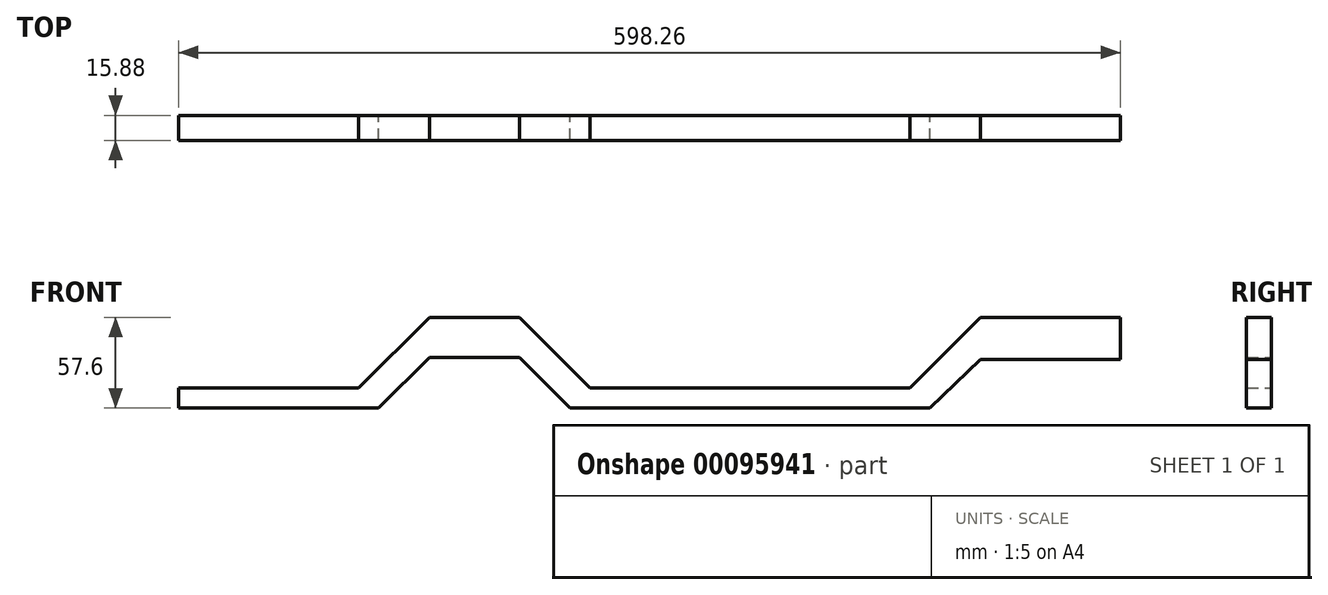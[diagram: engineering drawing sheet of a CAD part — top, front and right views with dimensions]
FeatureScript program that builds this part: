
annotation { "Feature Type Name" : "Feature", "Feature Type Description" : "" }
export const myFeature = defineFeature(function(context is Context, id is Id, definition is map)
    precondition{}
    {
        {
            var Q0;
            Q0=qCreatedBy(makeId("Front.planeOp"),FACE);
            var sketch = newSketch(context, id + "F0", { "sketchPlane" : qUnion([Q0])});
            skLineSegment(sketch, "E0", {"start": v(-232.76, -81.83) * mm, "end": v(-105.76, -81.83) * mm});
            skLineSegment(sketch, "E1", {"start": v(-105.76, -81.83) * mm, "end": v(-118.46, -69.13) * mm});
            skLineSegment(sketch, "E2", {"start": v(-118.46, -69.13) * mm, "end": v(-232.76, -69.13) * mm});
            skLineSegment(sketch, "E3", {"start": v(-118.46, -69.13) * mm, "end": v(-73.56, -24.23) * mm});
            skLineSegment(sketch, "E4", {"start": v(-105.76, -81.83) * mm, "end": v(-73.56, -49.63) * mm});
            skLineSegment(sketch, "E5", {"start": v(-73.56, -24.23) * mm, "end": v(-73.56, -49.63) * mm});
            skLineSegment(sketch, "E6", {"start": v(-73.56, -24.23) * mm, "end": v(-16.4, -24.23) * mm});
            skLineSegment(sketch, "E7", {"start": v(-73.56, -49.63) * mm, "end": v(-16.4, -49.63) * mm});
            skLineSegment(sketch, "E8", {"start": v(-16.4, -24.23) * mm, "end": v(-16.4, -49.63) * mm});
            skLineSegment(sketch, "E9", {"start": v(-16.4, -24.23) * mm, "end": v(28.5, -69.13) * mm});
            skLineSegment(sketch, "E10", {"start": v(28.5, -69.13) * mm, "end": v(53.9, -69.13) * mm});
            skLineSegment(sketch, "E11", {"start": v(53.9, -81.83) * mm, "end": v(15.8, -81.83) * mm});
            skLineSegment(sketch, "E12", {"start": v(15.8, -81.83) * mm, "end": v(28.5, -69.13) * mm});
            skLineSegment(sketch, "E13", {"start": v(-16.4, -49.63) * mm, "end": v(15.8, -81.83) * mm});
            skLineSegment(sketch, "E14", {"start": v(53.9, -81.83) * mm, "end": v(244.4, -81.83) * mm});
            skLineSegment(sketch, "E15", {"start": v(231.7, -69.14) * mm, "end": v(244.4, -81.83) * mm});
            skLineSegment(sketch, "E16", {"start": v(-232.76, -69.13) * mm, "end": v(-232.76, -81.83) * mm});
            skLineSegment(sketch, "E17", {"start": v(53.9, -69.13) * mm, "end": v(231.7, -69.14) * mm});
            skLineSegment(sketch, "E18", {"start": v(231.7, -69.14) * mm, "end": v(276.6, -24.23) * mm});
            skLineSegment(sketch, "E19", {"start": v(276.6, -24.23) * mm, "end": v(365.5, -24.23) * mm});
            skLineSegment(sketch, "E20", {"start": v(244.4, -81.83) * mm, "end": v(276.6, -50.74) * mm});
            skLineSegment(sketch, "E21", {"start": v(276.6, -24.23) * mm, "end": v(276.6, -50.74) * mm});
            skLineSegment(sketch, "E22", {"start": v(276.6, -50.74) * mm, "end": v(365.5, -50.74) * mm});
            skLineSegment(sketch, "E23", {"start": v(365.5, -50.74) * mm, "end": v(365.5, -24.23) * mm});
            skSolve(sketch);
        }
        {
            var Q0;
            Q0=makeQuery(id+"F0.imprint","IMPRINT",FACE,{"disambiguationData":[TD([[makeQuery(id+"F0.imprint","IMPRINT",EDGE,{"derivedFrom":sQuery(id+"F0.wireOp",EDGE,"E0")}),1.0]])]});
            extrude(context, id + "F1", {"entities" : qUnion([Q0]), "endBound" : BoundingType.SYMMETRIC, "depth" : 15.88 * mm});
        }
        {
            var Q0;
            Q0=makeQuery(id+"F0.imprint","IMPRINT",FACE,{"disambiguationData":[TD([[makeQuery(id+"F0.imprint","IMPRINT",EDGE,{"derivedFrom":sQuery(id+"F0.wireOp",EDGE,"E1")}),-1.0]])]});
            extrude(context, id + "F2", {"entities" : qUnion([Q0]), "operationType" : NewBodyOperationType.ADD, "endBound" : BoundingType.SYMMETRIC, "depth" : 15.88 * mm});
        }
        {
            var Q0;
            Q0=makeQuery(id+"F0.imprint","IMPRINT",FACE,{"disambiguationData":[TD([[makeQuery(id+"F0.imprint","IMPRINT",EDGE,{"derivedFrom":sQuery(id+"F0.wireOp",EDGE,"E5")}),1.0]])]});
            extrude(context, id + "F3", {"entities" : qUnion([Q0]), "operationType" : NewBodyOperationType.ADD, "endBound" : BoundingType.SYMMETRIC, "depth" : 15.88 * mm});
        }
        {
            var Q0;
            Q0=makeQuery(id+"F0.imprint","IMPRINT",FACE,{"disambiguationData":[TD([[makeQuery(id+"F0.imprint","IMPRINT",EDGE,{"derivedFrom":sQuery(id+"F0.wireOp",EDGE,"E8")}),1.0]])]});
            extrude(context, id + "F4", {"entities" : qUnion([Q0]), "operationType" : NewBodyOperationType.ADD, "endBound" : BoundingType.SYMMETRIC, "depth" : 15.88 * mm});
        }
        {
            var Q0;
            Q0=makeQuery(id+"F0.imprint","IMPRINT",FACE,{"disambiguationData":[TD([[makeQuery(id+"F0.imprint","IMPRINT",EDGE,{"derivedFrom":sQuery(id+"F0.wireOp",EDGE,"E10")}),-1.0]])]});
            extrude(context, id + "F5", {"entities" : qUnion([Q0]), "operationType" : NewBodyOperationType.ADD, "endBound" : BoundingType.SYMMETRIC, "depth" : 15.88 * mm});
        }
        {
            var Q0;
            Q0=makeQuery(id+"F0.imprint","IMPRINT",FACE,{"disambiguationData":[TD([[makeQuery(id+"F0.imprint","IMPRINT",EDGE,{"derivedFrom":sQuery(id+"F0.wireOp",EDGE,"E15")}),1.0]])]});
            extrude(context, id + "F6", {"entities" : qUnion([Q0]), "operationType" : NewBodyOperationType.ADD, "endBound" : BoundingType.SYMMETRIC, "depth" : 15.88 * mm});
        }
        {
            var Q0;
            Q0=makeQuery(id+"F0.imprint","IMPRINT",FACE,{"disambiguationData":[TD([[makeQuery(id+"F0.imprint","IMPRINT",EDGE,{"derivedFrom":sQuery(id+"F0.wireOp",EDGE,"E19")}),-1.0]])]});
            extrude(context, id + "F7", {"entities" : qUnion([Q0]), "operationType" : NewBodyOperationType.ADD, "endBound" : BoundingType.SYMMETRIC, "depth" : 15.88 * mm});
        }
    });
